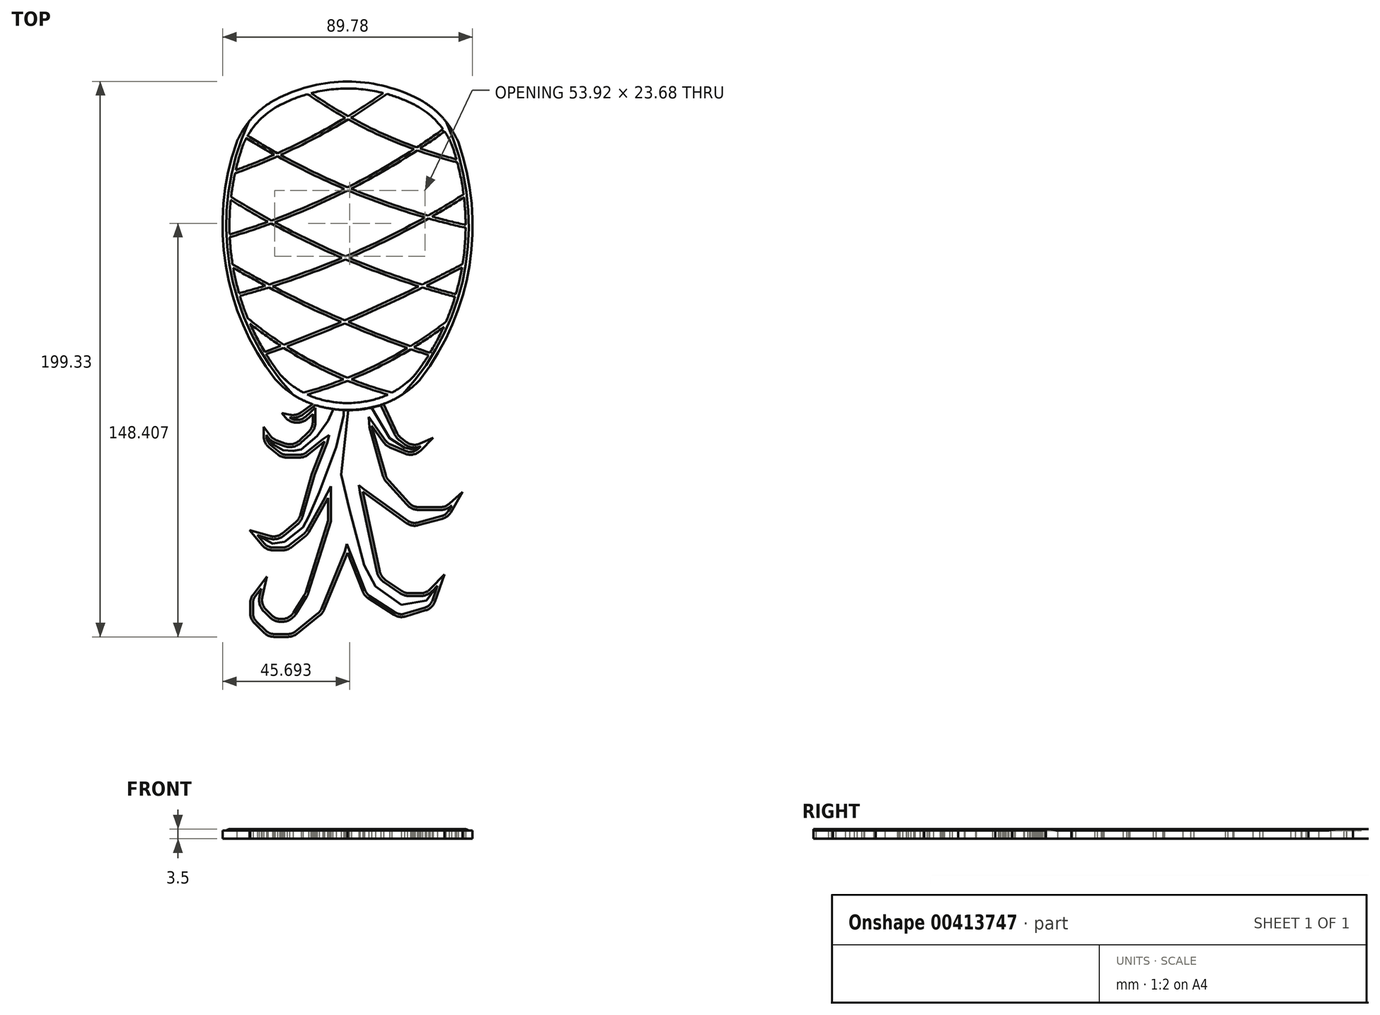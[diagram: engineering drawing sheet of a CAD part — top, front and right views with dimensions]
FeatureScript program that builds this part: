
annotation { "Feature Type Name" : "Feature", "Feature Type Description" : "" }
export const myFeature = defineFeature(function(context is Context, id is Id, definition is map)
    precondition{}
    {
        {
            var Q0;
            Q0=qCreatedBy(makeId("Top.planeOp"),FACE);
            var sketch = newSketch(context, id + "F0", { "sketchPlane" : qUnion([Q0])});
            skPoint(sketch, "E0.endSnap0", {"position": v(0.15, 19.93) * mm});
            skArc(sketch, "E1", {"start": v(-37.44, 35.3) * mm, "mid": v(-38.9, 30.75) * mm, "end": v(-40.1, 26.12) * mm});
            skPoint(sketch, "E2.center.orphan", {"position": v(0, -42.88) * mm});
            skArc(sketch, "E3", {"start": v(-24.09, -47.3) * mm, "mid": v(-20.2, -50.89) * mm, "end": v(-15.76, -53.75) * mm});
            skPoint(sketch, "E4.center.orphan", {"position": v(0, 37.68) * mm});
            skArc(sketch, "E5", {"start": v(-0.05, 55.44) * mm, "mid": v(-6.58, 55) * mm, "end": v(-13, 53.76) * mm});
            skArc(sketch, "E6", {"start": v(-23.24, 49.97) * mm, "mid": v(-30.39, 45.18) * mm, "end": v(-35.81, 38.5) * mm});
            skArc(sketch, "E7.MirrorCS", {"start": v(24.33, -47.22) * mm, "mid": v(20.41, -50.86) * mm, "end": v(15.91, -53.76) * mm});
            skArc(sketch, "E8.MirrorCS", {"start": v(37.4, 35.42) * mm, "mid": v(38.3, 32.73) * mm, "end": v(39.12, 30.01) * mm});
            skArc(sketch, "E9.MirrorCS", {"start": v(23.15, 50.05) * mm, "mid": v(29.32, 46.15) * mm, "end": v(34.32, 40.82) * mm});
            skArc(sketch, "E10.MirrorCS", {"start": v(-0.05, 55.44) * mm, "mid": v(6.47, 55.02) * mm, "end": v(12.9, 53.8) * mm});
            skArc(sketch, "E11", {"start": v(-5.74, -56.97) * mm, "mid": v(0, -57.48) * mm, "end": v(5.75, -56.99) * mm});
            skPoint(sketch, "E12.orphan", {"position": v(0.14, -57.2) * mm});
            skArc(sketch, "E13.0", {"start": v(24.2, 52.31) * mm, "mid": v(33.43, 45.75) * mm, "end": v(39.73, 36.34) * mm});
            skArc(sketch, "E13.1", {"start": v(39.73, 36.34) * mm, "mid": v(43.8, -7.95) * mm, "end": v(26.26, -48.81) * mm});
            skArc(sketch, "E13.2", {"start": v(26.26, -48.81) * mm, "mid": v(17.14, -55.93) * mm, "end": v(6.13, -59.46) * mm});
            skArc(sketch, "E13.3", {"start": v(-24.2, 52.28) * mm, "mid": v(-33.47, 45.67) * mm, "end": v(-39.77, 36.2) * mm});
            skArc(sketch, "E13.4", {"start": v(-39.77, 36.2) * mm, "mid": v(-43.7, -8.1) * mm, "end": v(-26, -48.9) * mm});
            skArc(sketch, "E13.5", {"start": v(-26, -48.9) * mm, "mid": v(-17, -55.93) * mm, "end": v(-6.13, -59.44) * mm});
            skArc(sketch, "E13.6", {"start": v(-6.13, -59.44) * mm, "mid": v(0, -59.98) * mm, "end": v(6.13, -59.46) * mm});
            skArc(sketch, "E14.0", {"start": v(-0.06, 57.94) * mm, "mid": v(13.5, 56.23) * mm, "end": v(26.25, 51.27) * mm});
            skArc(sketch, "E14.1", {"start": v(-0.06, 57.94) * mm, "mid": v(-13.62, 56.18) * mm, "end": v(-26.34, 51.18) * mm});
            skArc(sketch, "E15", {"start": v(-35.78, -27.03) * mm, "mid": v(-29.42, -31.97) * mm, "end": v(-22.8, -36.53) * mm});
            skArc(sketch, "E16", {"start": v(-41.23, -7.7) * mm, "mid": v(-34.7, -11.37) * mm, "end": v(-28.1, -14.91) * mm});
            skArc(sketch, "E17", {"start": v(-41.76, 16.52) * mm, "mid": v(-34.59, 12.19) * mm, "end": v(-27.3, 8.06) * mm});
            skArc(sketch, "E18", {"start": v(-35.81, 38.5) * mm, "mid": v(-30.5, 35.28) * mm, "end": v(-25.1, 32.2) * mm});
            skArc(sketch, "E19", {"start": v(-13, 53.76) * mm, "mid": v(-6.49, 49.47) * mm, "end": v(0.23, 45.5) * mm});
            skArc(sketch, "E20", {"start": v(-15.76, -53.75) * mm, "mid": v(-8.47, -51.53) * mm, "end": v(-1.3, -48.94) * mm});
            skArc(sketch, "E21", {"start": v(-29.7, -39.09) * mm, "mid": v(-26.83, -38.04) * mm, "end": v(-23.96, -36.97) * mm});
            skArc(sketch, "E22", {"start": v(-38.9, -18.07) * mm, "mid": v(-34.16, -16.74) * mm, "end": v(-29.45, -15.33) * mm});
            skArc(sketch, "E23", {"start": v(-42.3, 3.08) * mm, "mid": v(-35.39, 5.25) * mm, "end": v(-28.54, 7.6) * mm});
            skArc(sketch, "E24", {"start": v(-40.1, 26.12) * mm, "mid": v(-33.13, 28.8) * mm, "end": v(-26.25, 31.69) * mm});
            skArc(sketch, "E25.0", {"start": v(-34.94, -29) * mm, "mid": v(-29.55, -33.12) * mm, "end": v(-23.96, -36.97) * mm});
            skArc(sketch, "E26.0", {"start": v(-41.02, -8.97) * mm, "mid": v(-35.26, -12.2) * mm, "end": v(-29.45, -15.33) * mm});
            skArc(sketch, "E27.0", {"start": v(-41.89, 15.42) * mm, "mid": v(-35.26, 11.43) * mm, "end": v(-28.54, 7.6) * mm});
            skArc(sketch, "E28.0", {"start": v(-36.3, 37.63) * mm, "mid": v(-31.31, 34.6) * mm, "end": v(-26.25, 31.69) * mm});
            skArc(sketch, "E29.0", {"start": v(-13.57, 52.94) * mm, "mid": v(-7.26, 48.77) * mm, "end": v(-0.76, 44.9) * mm});
            skArc(sketch, "E30.0", {"start": v(-39.75, 25.18) * mm, "mid": v(-32.4, 28) * mm, "end": v(-25.16, 31.08) * mm});
            skArc(sketch, "E31.0", {"start": v(-42.01, 2.12) * mm, "mid": v(-34.66, 4.43) * mm, "end": v(-27.37, 6.97) * mm});
            skArc(sketch, "E32.0", {"start": v(-38.64, -19.03) * mm, "mid": v(-33.4, -17.56) * mm, "end": v(-28.2, -16) * mm});
            skArc(sketch, "E33.0", {"start": v(-29.17, -39.96) * mm, "mid": v(-26.04, -38.81) * mm, "end": v(-22.91, -37.65) * mm});
            skArc(sketch, "E34.0", {"start": v(-14.43, -54.41) * mm, "mid": v(-7.13, -52.13) * mm, "end": v(0.03, -49.49) * mm});
            skLineSegment(sketch, "E35", {"start": v(38.87, 29.05) * mm, "end": v(39.43, 28.9) * mm});
            skLineSegment(sketch, "E36", {"start": v(42.2, 5.49) * mm, "end": v(42.42, 5.44) * mm});
            skLineSegment(sketch, "E37", {"start": v(-13.57, 52.94) * mm, "end": v(-14.4, 53.38) * mm});
            skArc(sketch, "E38.trimOffspring", {"start": v(-14.4, 53.38) * mm, "mid": v(-19.9, 51.47) * mm, "end": v(-25.15, 48.98) * mm});
            skArc(sketch, "E39.trimOffspring", {"start": v(-25.16, 31.08) * mm, "mid": v(-13.28, 24.9) * mm, "end": v(-1.1, 19.37) * mm});
            skArc(sketch, "E40.trimOffspring", {"start": v(-25.1, 32.2) * mm, "mid": v(-12.74, 38.18) * mm, "end": v(-0.76, 44.9) * mm});
            skArc(sketch, "E41.trimOffspring", {"start": v(-24.02, 31.6) * mm, "mid": v(-12.09, 25.44) * mm, "end": v(0.15, 19.93) * mm});
            skArc(sketch, "E42.trimOffspring", {"start": v(-24.02, 31.6) * mm, "mid": v(-11.7, 37.6) * mm, "end": v(0.25, 44.35) * mm});
            skLineSegment(sketch, "E43", {"start": v(-39.75, 25.18) * mm, "end": v(-40.36, 24.97) * mm});
            skLineSegment(sketch, "E44", {"start": v(-42.01, 2.12) * mm, "end": v(-42.25, 2.05) * mm});
            skArc(sketch, "E45.trimOffspring", {"start": v(29.1, -40.32) * mm, "mid": v(26.8, -43.82) * mm, "end": v(24.33, -47.22) * mm});
            skArc(sketch, "E46.trimOffspring", {"start": v(34.54, -30.19) * mm, "mid": v(32.23, -34.89) * mm, "end": v(29.65, -39.44) * mm});
            skArc(sketch, "E47.trimOffspring", {"start": v(38.62, -19.38) * mm, "mid": v(37.12, -23.89) * mm, "end": v(35.37, -28.3) * mm});
            skArc(sketch, "E48.trimOffspring", {"start": v(41.14, -8.8) * mm, "mid": v(40.16, -13.64) * mm, "end": v(38.9, -18.42) * mm});
            skArc(sketch, "E49.trimOffspring", {"start": v(42.42, 5.44) * mm, "mid": v(42.12, -1.08) * mm, "end": v(41.34, -7.55) * mm});
            skArc(sketch, "E50.trimOffspring", {"start": v(41.83, 16.36) * mm, "mid": v(42.26, 11.42) * mm, "end": v(42.42, 6.47) * mm});
            skArc(sketch, "E51.trimOffspring", {"start": v(39.43, 28.9) * mm, "mid": v(40.75, 23.22) * mm, "end": v(41.7, 17.46) * mm});
            skArc(sketch, "E52.trimOffspring", {"start": v(34.9, 40) * mm, "mid": v(36.25, 37.77) * mm, "end": v(37.4, 35.42) * mm});
            skLineSegment(sketch, "E53", {"start": v(13.47, 52.98) * mm, "end": v(14.16, 53.47) * mm});
            skArc(sketch, "E54.trimOffspring", {"start": v(14.16, 53.47) * mm, "mid": v(19.73, 51.57) * mm, "end": v(25.06, 49.07) * mm});
            skArc(sketch, "E55.trimOffspring", {"start": v(-36.3, 37.63) * mm, "mid": v(-36.9, 36.48) * mm, "end": v(-37.44, 35.3) * mm});
            skArc(sketch, "E56.trimOffspring", {"start": v(-40.36, 24.97) * mm, "mid": v(-41.16, 20.76) * mm, "end": v(-41.76, 16.52) * mm});
            skArc(sketch, "E57.trimOffspring", {"start": v(-41.89, 15.42) * mm, "mid": v(-42.3, 9.26) * mm, "end": v(-42.3, 3.08) * mm});
            skArc(sketch, "E58.trimOffspring", {"start": v(-42.25, 2.05) * mm, "mid": v(-41.88, -2.84) * mm, "end": v(-41.23, -7.7) * mm});
            skArc(sketch, "E59.trimOffspring", {"start": v(-41.02, -8.97) * mm, "mid": v(-40.08, -13.55) * mm, "end": v(-38.9, -18.07) * mm});
            skArc(sketch, "E60.trimOffspring", {"start": v(-38.62, -19.03) * mm, "mid": v(-37.3, -23.06) * mm, "end": v(-35.78, -27.03) * mm});
            skArc(sketch, "E61.trimOffspring", {"start": v(-34.94, -29) * mm, "mid": v(-32.49, -34.13) * mm, "end": v(-29.7, -39.09) * mm});
            skArc(sketch, "E62.trimOffspring", {"start": v(-29.17, -39.96) * mm, "mid": v(-26.72, -43.7) * mm, "end": v(-24.09, -47.3) * mm});
            skArc(sketch, "E63.trimOffspring", {"start": v(-14.43, -54.41) * mm, "mid": v(-10.18, -56.02) * mm, "end": v(-5.74, -56.97) * mm});
            skPoint(sketch, "E64.trimOffspring.end.orphan", {"position": v(0.15, -64.2) * mm});
            skArc(sketch, "E65.trimOffspring", {"start": v(0.04, -48.4) * mm, "mid": v(11, -43.5) * mm, "end": v(21.54, -37.71) * mm});
            skArc(sketch, "E66.trimOffspring", {"start": v(0.03, -49.49) * mm, "mid": v(7.23, -52.16) * mm, "end": v(14.56, -54.42) * mm});
            skArc(sketch, "E67.trimOffspring", {"start": v(1.38, -48.94) * mm, "mid": v(12.28, -43.97) * mm, "end": v(22.76, -38.14) * mm});
            skArc(sketch, "E68.trimOffspring", {"start": v(1.38, -48.94) * mm, "mid": v(8.58, -51.55) * mm, "end": v(15.91, -53.76) * mm});
            skArc(sketch, "E69.trimOffspring", {"start": v(-22.8, -36.53) * mm, "mid": v(-12.5, -32.54) * mm, "end": v(-2.3, -28.34) * mm});
            skArc(sketch, "E70.trimOffspring", {"start": v(-21.74, -37.2) * mm, "mid": v(-11.34, -33.15) * mm, "end": v(-1.02, -28.88) * mm});
            skArc(sketch, "E71.trimOffspring", {"start": v(-21.74, -37.2) * mm, "mid": v(-11.1, -43.3) * mm, "end": v(0.04, -48.4) * mm});
            skArc(sketch, "E72.trimOffspring", {"start": v(-22.91, -37.65) * mm, "mid": v(-12.36, -43.77) * mm, "end": v(-1.3, -48.94) * mm});
            skArc(sketch, "E73.trimOffspring", {"start": v(23.86, -37.47) * mm, "mid": v(26.75, -38.47) * mm, "end": v(29.65, -39.44) * mm});
            skArc(sketch, "E74.trimOffspring", {"start": v(22.76, -38.14) * mm, "mid": v(25.93, -39.24) * mm, "end": v(29.1, -40.32) * mm});
            skArc(sketch, "E75.trimOffspring", {"start": v(22.64, -37.04) * mm, "mid": v(29.12, -32.84) * mm, "end": v(35.37, -28.3) * mm});
            skArc(sketch, "E76.trimOffspring", {"start": v(23.86, -37.47) * mm, "mid": v(29.28, -33.94) * mm, "end": v(34.54, -30.19) * mm});
            skArc(sketch, "E77.trimOffspring", {"start": v(0.25, -28.34) * mm, "mid": v(13.7, -22.36) * mm, "end": v(27, -16.03) * mm});
            skArc(sketch, "E78.trimOffspring", {"start": v(-1.02, -28.88) * mm, "mid": v(10.19, -33.47) * mm, "end": v(21.54, -37.71) * mm});
            skArc(sketch, "E79.trimOffspring", {"start": v(-1.02, -27.8) * mm, "mid": v(12.37, -21.87) * mm, "end": v(25.61, -15.6) * mm});
            skArc(sketch, "E80.trimOffspring", {"start": v(0.25, -28.34) * mm, "mid": v(11.38, -32.87) * mm, "end": v(22.64, -37.04) * mm});
            skArc(sketch, "E81.trimOffspring", {"start": v(-28.1, -14.91) * mm, "mid": v(-14.92, -10.45) * mm, "end": v(-1.97, -5.36) * mm});
            skArc(sketch, "E82.trimOffspring", {"start": v(-26.84, -15.57) * mm, "mid": v(-13.65, -11.05) * mm, "end": v(-0.69, -5.9) * mm});
            skArc(sketch, "E83.trimOffspring", {"start": v(-28.2, -16) * mm, "mid": v(-15.36, -22.4) * mm, "end": v(-2.3, -28.34) * mm});
            skArc(sketch, "E84.trimOffspring", {"start": v(-26.84, -15.57) * mm, "mid": v(-14.05, -21.92) * mm, "end": v(-1.02, -27.8) * mm});
            skArc(sketch, "E85.trimOffspring", {"start": v(-27.3, 8.06) * mm, "mid": v(-14.04, 13.35) * mm, "end": v(-1.1, 19.37) * mm});
            skArc(sketch, "E86.trimOffspring", {"start": v(-26.12, 7.43) * mm, "mid": v(-12.84, 12.77) * mm, "end": v(0.12, 18.86) * mm});
            skArc(sketch, "E87.trimOffspring", {"start": v(-27.37, 6.97) * mm, "mid": v(-14.82, 0.5) * mm, "end": v(-1.97, -5.36) * mm});
            skArc(sketch, "E88.trimOffspring", {"start": v(-26.12, 7.43) * mm, "mid": v(-13.55, 1) * mm, "end": v(-0.69, -4.82) * mm});
            skArc(sketch, "E89.trimOffspring", {"start": v(0.6, -5.36) * mm, "mid": v(13.64, -10.47) * mm, "end": v(26.91, -14.95) * mm});
            skArc(sketch, "E90.trimOffspring", {"start": v(0.6, -5.36) * mm, "mid": v(15.06, 1.32) * mm, "end": v(29.15, 8.78) * mm});
            skArc(sketch, "E91.trimOffspring", {"start": v(-0.69, -5.9) * mm, "mid": v(12.35, -11.06) * mm, "end": v(25.61, -15.6) * mm});
            skArc(sketch, "E92.trimOffspring", {"start": v(-0.69, -4.82) * mm, "mid": v(13.74, 1.79) * mm, "end": v(27.8, 9.16) * mm});
            skArc(sketch, "E93.trimOffspring", {"start": v(27, -16.03) * mm, "mid": v(32.8, -17.76) * mm, "end": v(38.65, -19.39) * mm});
            skArc(sketch, "E94.trimOffspring", {"start": v(28.3, -15.38) * mm, "mid": v(33.59, -16.95) * mm, "end": v(38.9, -18.42) * mm});
            skArc(sketch, "E95.trimOffspring", {"start": v(28.3, -15.38) * mm, "mid": v(34.74, -12.13) * mm, "end": v(41.14, -8.8) * mm});
            skArc(sketch, "E96.trimOffspring", {"start": v(26.91, -14.95) * mm, "mid": v(34.15, -11.3) * mm, "end": v(41.34, -7.55) * mm});
            skArc(sketch, "E97.trimOffspring", {"start": v(29.02, 9.85) * mm, "mid": v(35.4, 13.58) * mm, "end": v(41.7, 17.46) * mm});
            skArc(sketch, "E98.trimOffspring", {"start": v(29.15, 8.78) * mm, "mid": v(35.65, 7.05) * mm, "end": v(42.2, 5.49) * mm});
            skArc(sketch, "E99.trimOffspring", {"start": v(30.38, 9.48) * mm, "mid": v(36.14, 12.85) * mm, "end": v(41.83, 16.36) * mm});
            skArc(sketch, "E100.trimOffspring", {"start": v(30.38, 9.48) * mm, "mid": v(36.38, 7.9) * mm, "end": v(42.42, 6.47) * mm});
            skArc(sketch, "E101.trimOffspring", {"start": v(1.3, 19.45) * mm, "mid": v(18.5, 29.08) * mm, "end": v(34.9, 40) * mm});
            skArc(sketch, "E102.trimOffspring", {"start": v(1.3, 19.45) * mm, "mid": v(15.02, 14.25) * mm, "end": v(29.02, 9.85) * mm});
            skArc(sketch, "E103.trimOffspring", {"start": v(0.12, 18.86) * mm, "mid": v(13.82, 13.6) * mm, "end": v(27.8, 9.16) * mm});
            skArc(sketch, "E104.trimOffspring", {"start": v(0.08, 19.96) * mm, "mid": v(17.61, 29.71) * mm, "end": v(34.32, 40.82) * mm});
            skArc(sketch, "E105.trimOffspring", {"start": v(1.23, 44.94) * mm, "mid": v(7.42, 48.87) * mm, "end": v(13.47, 52.98) * mm});
            skArc(sketch, "E106.trimOffspring", {"start": v(1.23, 44.94) * mm, "mid": v(19.7, 36.27) * mm, "end": v(39.12, 30.01) * mm});
            skArc(sketch, "E107.trimOffspring", {"start": v(0.23, 45.5) * mm, "mid": v(6.63, 49.55) * mm, "end": v(12.9, 53.8) * mm});
            skArc(sketch, "E108.trimOffspring", {"start": v(0.25, 44.35) * mm, "mid": v(19.07, 35.45) * mm, "end": v(38.87, 29.05) * mm});
            skArc(sketch, "E109.trimOffspring", {"start": v(14.56, -54.42) * mm, "mid": v(10.26, -56.04) * mm, "end": v(5.75, -56.99) * mm});
            skLineSegment(sketch, "E110", {"start": v(15.91, -53.76) * mm, "end": v(14.56, -54.42) * mm});
            skLineSegment(sketch, "E111", {"start": v(-14.43, -54.41) * mm, "end": v(-15.76, -53.75) * mm});
            skLineSegment(sketch, "E112", {"start": v(-29.17, -39.96) * mm, "end": v(-29.7, -39.09) * mm});
            skLineSegment(sketch, "E113", {"start": v(-34.94, -29) * mm, "end": v(-35.78, -27.03) * mm});
            skLineSegment(sketch, "E114", {"start": v(-38.64, -19.03) * mm, "end": v(-38.9, -18.07) * mm});
            skLineSegment(sketch, "E115", {"start": v(-41.02, -8.97) * mm, "end": v(-41.23, -7.7) * mm});
            skLineSegment(sketch, "E116", {"start": v(-42.25, 2.05) * mm, "end": v(-42.3, 3.08) * mm});
            skLineSegment(sketch, "E117", {"start": v(-41.89, 15.42) * mm, "end": v(-41.76, 16.52) * mm});
            skLineSegment(sketch, "E118", {"start": v(-40.36, 24.97) * mm, "end": v(-40.1, 26.12) * mm});
            skLineSegment(sketch, "E119", {"start": v(-36.3, 37.63) * mm, "end": v(-35.81, 38.5) * mm});
            skLineSegment(sketch, "E120", {"start": v(-14.4, 53.38) * mm, "end": v(-13, 53.76) * mm});
            skLineSegment(sketch, "E121", {"start": v(12.9, 53.8) * mm, "end": v(14.16, 53.47) * mm});
            skLineSegment(sketch, "E122", {"start": v(34.32, 40.82) * mm, "end": v(34.9, 40) * mm});
            skLineSegment(sketch, "E123", {"start": v(39.12, 30.01) * mm, "end": v(39.43, 28.9) * mm});
            skLineSegment(sketch, "E124", {"start": v(41.7, 17.46) * mm, "end": v(41.83, 16.36) * mm});
            skLineSegment(sketch, "E125", {"start": v(42.42, 6.47) * mm, "end": v(42.42, 5.44) * mm});
            skLineSegment(sketch, "E126", {"start": v(41.34, -7.55) * mm, "end": v(41.14, -8.8) * mm});
            skLineSegment(sketch, "E127", {"start": v(38.62, -19.38) * mm, "end": v(38.9, -18.42) * mm});
            skLineSegment(sketch, "E128", {"start": v(35.37, -28.3) * mm, "end": v(34.54, -30.19) * mm});
            skLineSegment(sketch, "E129", {"start": v(29.65, -39.44) * mm, "end": v(29.1, -40.32) * mm});
            skSolve(sketch);
        }
        {
            var Q0;
            Q0 = qSketchRegion(id + "F0", true);
            var Q1;
            Q1=makeQuery(id+"F0.imprint","IMPRINT",FACE,{"disambiguationData":[TD([[makeQuery(id+"F0.imprint","IMPRINT",EDGE,{"derivedFrom":sQuery(id+"F0.wireOp",EDGE,"E1")}),-1.0]])]});
            var Q2;
            Q2=makeQuery(id+"F0.imprint","IMPRINT",FACE,{"disambiguationData":[TD([[makeQuery(id+"F0.imprint","IMPRINT",EDGE,{"derivedFrom":sQuery(id+"F0.wireOp",EDGE,"E15")}),-1.0]])]});
            var Q3;
            {var subQ5=sQuery(id+"F0.wireOp",EDGE,"E122");Q3=makeQuery(id+"F0.imprint","IMPRINT",FACE,{"disambiguationData":[TD([[makeQuery(id+"F0.imprint","IMPRINT",EDGE,{"derivedFrom":subQ5}),-1.0]])]});}
            var Q4;
            {var subQ0=sQuery(id+"F0.wireOp",EDGE,"E108.trimOffspring");var subQ1=sQuery(id+"F0.wireOp",EDGE,"E101.trimOffspring");var subQ2=makeQuery(id+"F0.imprint","INTERSECT",VERTEX,{"derivedFrom":[subQ1,subQ0]});Q4=makeQuery(id+"F0.imprint","IMPRINT",FACE,{"disambiguationData":[TD([[makeQuery(id+"F0.imprint","IMPRINT",EDGE,{"disambiguationData":[TD([[subQ2,-1.0]])],"derivedFrom":subQ1}),1.0]])]});}
            var Q5;
            {var subQ6=sQuery(id+"F0.wireOp",EDGE,"E35");Q5=makeQuery(id+"F0.imprint","IMPRINT",FACE,{"disambiguationData":[TD([[makeQuery(id+"F0.imprint","IMPRINT",EDGE,{"derivedFrom":subQ6}),1.0]])]});}
            extrude(context, id + "F1", {"entities" : qUnion([Q0, Q1, Q2, Q3, Q4, Q5]), "depth" : 3.5 * mm});
        }
        {
            var Q0;
            {var subQ1=sQuery(id+"F0.wireOp",EDGE,"E18");Q0=makeQuery(id+"F0.imprint","IMPRINT",FACE,{"disambiguationData":[TD([[makeQuery(id+"F0.imprint","IMPRINT",EDGE,{"derivedFrom":subQ1}),1.0]])]});}
            var Q1;
            Q1=makeQuery(id+"F0.imprint","IMPRINT",FACE,{"disambiguationData":[TD([[makeQuery(id+"F0.imprint","IMPRINT",EDGE,{"derivedFrom":sQuery(id+"F0.wireOp",EDGE,"E5")}),1.0]])]});
            var Q2;
            {var subQ5=sQuery(id+"F0.wireOp",EDGE,"E53");Q2=makeQuery(id+"F0.imprint","IMPRINT",FACE,{"disambiguationData":[TD([[makeQuery(id+"F0.imprint","IMPRINT",EDGE,{"derivedFrom":subQ5}),-1.0]])]});}
            var Q3;
            {var subQ0=sQuery(id+"F0.wireOp",EDGE,"E42.trimOffspring");Q3=makeQuery(id+"F0.imprint","IMPRINT",FACE,{"disambiguationData":[TD([[makeQuery(id+"F0.imprint","IMPRINT",EDGE,{"derivedFrom":subQ0}),-1.0]])]});}
            var Q4;
            {var subQ4=sQuery(id+"F0.wireOp",EDGE,"E35");Q4=makeQuery(id+"F0.imprint","IMPRINT",FACE,{"disambiguationData":[TD([[makeQuery(id+"F0.imprint","IMPRINT",EDGE,{"derivedFrom":subQ4}),-1.0]])]});}
            var Q5;
            {var subQ0=sQuery(id+"F0.wireOp",EDGE,"E8.MirrorCS");Q5=makeQuery(id+"F0.imprint","IMPRINT",FACE,{"disambiguationData":[TD([[makeQuery(id+"F0.imprint","IMPRINT",EDGE,{"derivedFrom":subQ0}),-1.0]])]});}
            var Q6;
            Q6=makeQuery(id+"F0.imprint","IMPRINT",FACE,{"disambiguationData":[TD([[makeQuery(id+"F0.imprint","IMPRINT",EDGE,{"derivedFrom":sQuery(id+"F0.wireOp",EDGE,"E1")}),1.0]])]});
            var Q7;
            Q7=makeQuery(id+"F0.imprint","IMPRINT",FACE,{"disambiguationData":[TD([[makeQuery(id+"F0.imprint","IMPRINT",EDGE,{"derivedFrom":sQuery(id+"F0.wireOp",EDGE,"E23")}),1.0]])]});
            var Q8;
            Q8=makeQuery(id+"F0.imprint","IMPRINT",FACE,{"disambiguationData":[TD([[makeQuery(id+"F0.imprint","IMPRINT",EDGE,{"derivedFrom":sQuery(id+"F0.wireOp",EDGE,"E16")}),1.0]])]});
            var Q9;
            Q9=makeQuery(id+"F0.imprint","IMPRINT",FACE,{"disambiguationData":[TD([[makeQuery(id+"F0.imprint","IMPRINT",EDGE,{"derivedFrom":sQuery(id+"F0.wireOp",EDGE,"E22")}),1.0]])]});
            var Q10;
            Q10=makeQuery(id+"F0.imprint","IMPRINT",FACE,{"disambiguationData":[TD([[makeQuery(id+"F0.imprint","IMPRINT",EDGE,{"derivedFrom":sQuery(id+"F0.wireOp",EDGE,"E15")}),1.0]])]});
            var Q11;
            Q11=makeQuery(id+"F0.imprint","IMPRINT",FACE,{"disambiguationData":[TD([[makeQuery(id+"F0.imprint","IMPRINT",EDGE,{"derivedFrom":sQuery(id+"F0.wireOp",EDGE,"E21")}),1.0]])]});
            var Q12;
            {var subQ0=sQuery(id+"F0.wireOp",EDGE,"E47.trimOffspring");Q12=makeQuery(id+"F0.imprint","IMPRINT",FACE,{"disambiguationData":[TD([[makeQuery(id+"F0.imprint","IMPRINT",EDGE,{"derivedFrom":subQ0}),-1.0]])]});}
            var Q13;
            Q13=makeQuery(id+"F0.imprint","IMPRINT",FACE,{"disambiguationData":[TD([[makeQuery(id+"F0.imprint","IMPRINT",EDGE,{"derivedFrom":sQuery(id+"F0.wireOp",EDGE,"E79.trimOffspring")}),1.0]])]});
            var Q14;
            Q14=makeQuery(id+"F0.imprint","IMPRINT",FACE,{"disambiguationData":[TD([[makeQuery(id+"F0.imprint","IMPRINT",EDGE,{"derivedFrom":sQuery(id+"F0.wireOp",EDGE,"E36")}),-1.0]])]});
            var Q15;
            Q15=makeQuery(id+"F0.imprint","IMPRINT",FACE,{"disambiguationData":[TD([[makeQuery(id+"F0.imprint","IMPRINT",EDGE,{"derivedFrom":sQuery(id+"F0.wireOp",EDGE,"E86.trimOffspring")}),-1.0]])]});
            var Q16;
            Q16=makeQuery(id+"F0.imprint","IMPRINT",FACE,{"disambiguationData":[TD([[makeQuery(id+"F0.imprint","IMPRINT",EDGE,{"derivedFrom":sQuery(id+"F0.wireOp",EDGE,"E17")}),1.0]])]});
            var Q17;
            Q17=makeQuery(id+"F0.imprint","IMPRINT",FACE,{"disambiguationData":[TD([[makeQuery(id+"F0.imprint","IMPRINT",EDGE,{"derivedFrom":sQuery(id+"F0.wireOp",EDGE,"E46.trimOffspring")}),-1.0]])]});
            var Q18;
            Q18=makeQuery(id+"F0.imprint","IMPRINT",FACE,{"disambiguationData":[TD([[makeQuery(id+"F0.imprint","IMPRINT",EDGE,{"derivedFrom":sQuery(id+"F0.wireOp",EDGE,"E48.trimOffspring")}),-1.0]])]});
            var Q19;
            Q19=makeQuery(id+"F0.imprint","IMPRINT",FACE,{"disambiguationData":[TD([[makeQuery(id+"F0.imprint","IMPRINT",EDGE,{"derivedFrom":sQuery(id+"F0.wireOp",EDGE,"E50.trimOffspring")}),-1.0]])]});
            var Q20;
            Q20=makeQuery(id+"F0.imprint","IMPRINT",FACE,{"disambiguationData":[TD([[makeQuery(id+"F0.imprint","IMPRINT",EDGE,{"derivedFrom":sQuery(id+"F0.wireOp",EDGE,"E3")}),1.0]])]});
            var Q21;
            Q21=makeQuery(id+"F0.imprint","IMPRINT",FACE,{"disambiguationData":[TD([[makeQuery(id+"F0.imprint","IMPRINT",EDGE,{"derivedFrom":sQuery(id+"F0.wireOp",EDGE,"E65.trimOffspring")}),1.0]])]});
            var Q22;
            Q22=makeQuery(id+"F0.imprint","IMPRINT",FACE,{"disambiguationData":[TD([[makeQuery(id+"F0.imprint","IMPRINT",EDGE,{"derivedFrom":sQuery(id+"F0.wireOp",EDGE,"E7.MirrorCS")}),-1.0]])]});
            var Q23;
            Q23=makeQuery(id+"F0.imprint","IMPRINT",FACE,{"disambiguationData":[TD([[makeQuery(id+"F0.imprint","IMPRINT",EDGE,{"derivedFrom":sQuery(id+"F0.wireOp",EDGE,"E11")}),1.0]])]});
            extrude(context, id + "F2", {"entities" : qUnion([Q0, Q1, Q2, Q3, Q4, Q5, Q6, Q7, Q8, Q9, Q10, Q11, Q12, Q13, Q14, Q15, Q16, Q17, Q18, Q19, Q20, Q21, Q22, Q23]), "depth" : 3 * mm});
        }
        {
            var Q0;
            Q0=makeQuery(id+"F1.opExtrude","CAP_EDGE",EDGE,{"disambiguationData":[OSD([sQuery(id+"F0.wireOp",EDGE,"E13.1")])],"isStart":false});
            fillet(context, id + "F3", {"entities" : qUnion([Q0]), "radius" : 3 * mm, "tangentPropagation" : true, "allowEdgeOverflow" : false});
        }
        {
            var Q0;
            Q0=makeQuery(id+"F1.opExtrude","CAP_EDGE",EDGE,{"disambiguationData":[OSD([sQuery(id+"F0.wireOp",EDGE,"E13.4")])],"isStart":false});
            fillet(context, id + "F4", {"entities" : qUnion([Q0]), "radius" : 3 * mm, "tangentPropagation" : true, "allowEdgeOverflow" : false});
        }
        {
            var Q0;
            Q0=qCreatedBy(makeId("Top.planeOp"),FACE);
            var sketch = newSketch(context, id + "F5", { "sketchPlane" : qUnion([Q0])});
            skArc(sketch, "E130", {"start": v(-12.47, -57.76) * mm, "mid": v(0.25, -60.04) * mm, "end": v(12.98, -57.88) * mm});
            skLineSegment(sketch, "E131", {"start": v(12.98, -57.88) * mm, "end": v(17.84, -68.25) * mm});
            skLineSegment(sketch, "E132", {"start": v(19.33, -70.1) * mm, "end": v(21.06, -71.42) * mm});
            skLineSegment(sketch, "E133", {"start": v(26.1, -72.04) * mm, "end": v(30.81, -70) * mm});
            skLineSegment(sketch, "E134", {"start": v(30.81, -70) * mm, "end": v(26.14, -74.6) * mm});
            skLineSegment(sketch, "E135", {"start": v(20.7, -75.64) * mm, "end": v(15.13, -73.32) * mm});
            skLineSegment(sketch, "E136", {"start": v(13, -71.62) * mm, "end": v(8.7, -65.63) * mm});
            skLineSegment(sketch, "E137", {"start": v(8.7, -65.63) * mm, "end": v(13.74, -83.35) * mm});
            skLineSegment(sketch, "E138", {"start": v(14.85, -85.34) * mm, "end": v(21.99, -93.22) * mm});
            skLineSegment(sketch, "E139", {"start": v(25.7, -94.86) * mm, "end": v(33.32, -94.86) * mm});
            skLineSegment(sketch, "E140", {"start": v(36.65, -93.6) * mm, "end": v(41.36, -89.4) * mm});
            skLineSegment(sketch, "E141", {"start": v(41.36, -89.4) * mm, "end": v(37.09, -96.73) * mm});
            skLineSegment(sketch, "E142", {"start": v(34.05, -99.04) * mm, "end": v(25.34, -101.35) * mm});
            skLineSegment(sketch, "E143", {"start": v(21.14, -100.58) * mm, "end": v(5.46, -89.3) * mm});
            skLineSegment(sketch, "E144", {"start": v(5.46, -89.3) * mm, "end": v(11.6, -117.88) * mm});
            skLineSegment(sketch, "E145", {"start": v(13.66, -120.96) * mm, "end": v(19.41, -124.89) * mm});
            skLineSegment(sketch, "E146", {"start": v(22.23, -125.76) * mm, "end": v(26.18, -125.76) * mm});
            skLineSegment(sketch, "E147", {"start": v(29.78, -124.22) * mm, "end": v(34.77, -119.03) * mm});
            skLineSegment(sketch, "E148", {"start": v(34.77, -119.03) * mm, "end": v(31.4, -128.7) * mm});
            skLineSegment(sketch, "E149", {"start": v(28.14, -131.84) * mm, "end": v(20.83, -134.08) * mm});
            skLineSegment(sketch, "E150", {"start": v(16.65, -133.5) * mm, "end": v(7.4, -127.5) * mm});
            skLineSegment(sketch, "E151", {"start": v(5.46, -125.13) * mm, "end": v(0, -111.21) * mm});
            skLineSegment(sketch, "E152", {"start": v(0, -111.21) * mm, "end": v(-8.44, -131.75) * mm});
            skLineSegment(sketch, "E153", {"start": v(-9.95, -133.76) * mm, "end": v(-18.15, -140.3) * mm});
            skLineSegment(sketch, "E154", {"start": v(-21.27, -141.39) * mm, "end": v(-26.4, -141.39) * mm});
            skLineSegment(sketch, "E155", {"start": v(-29.92, -139.95) * mm, "end": v(-33.4, -136.52) * mm});
            skLineSegment(sketch, "E156", {"start": v(-34.9, -132.95) * mm, "end": v(-34.9, -129.3) * mm});
            skLineSegment(sketch, "E157", {"start": v(-33.88, -126.28) * mm, "end": v(-28.98, -119.8) * mm});
            skLineSegment(sketch, "E158", {"start": v(-28.98, -119.8) * mm, "end": v(-30.57, -127.08) * mm});
            skLineSegment(sketch, "E159", {"start": v(-29.18, -131.73) * mm, "end": v(-27.24, -133.62) * mm});
            skLineSegment(sketch, "E160", {"start": v(-23.75, -135.03) * mm, "end": v(-23.6, -135.03) * mm});
            skLineSegment(sketch, "E161", {"start": v(-19.35, -132.67) * mm, "end": v(-15.5, -126.46) * mm});
            skLineSegment(sketch, "E162", {"start": v(-14.97, -125.31) * mm, "end": v(-6.97, -99.73) * mm});
            skLineSegment(sketch, "E163", {"start": v(-6.97, -99.73) * mm, "end": v(-6.97, -91.59) * mm});
            skLineSegment(sketch, "E164", {"start": v(-6.97, -91.59) * mm, "end": v(-13.82, -103.79) * mm});
            skLineSegment(sketch, "E165", {"start": v(-15.1, -105.28) * mm, "end": v(-20.22, -109.28) * mm});
            skLineSegment(sketch, "E166", {"start": v(-23.3, -110.33) * mm, "end": v(-26.74, -110.33) * mm});
            skLineSegment(sketch, "E167", {"start": v(-30.58, -108.54) * mm, "end": v(-35.15, -103.06) * mm});
            skLineSegment(sketch, "E168", {"start": v(-35.15, -103.06) * mm, "end": v(-27.87, -105.16) * mm});
            skPoint(sketch, "E168.endSnap0", {"position": v(-25.33, -110.33) * mm});
            skLineSegment(sketch, "E169", {"start": v(-23.3, -104.2) * mm, "end": v(-18.65, -100.33) * mm});
            skLineSegment(sketch, "E170", {"start": v(-17.04, -97.85) * mm, "end": v(-12.78, -82.86) * mm});
            skLineSegment(sketch, "E171", {"start": v(-12.78, -82.86) * mm, "end": v(-8.19, -71.23) * mm});
            skLineSegment(sketch, "E172", {"start": v(-8.19, -71.23) * mm, "end": v(-14.05, -75.94) * mm});
            skPoint(sketch, "E172.endSnap0", {"position": v(-10.48, -77.04) * mm});
            skLineSegment(sketch, "E173", {"start": v(-17.18, -77.04) * mm, "end": v(-21.87, -77.04) * mm});
            skLineSegment(sketch, "E174", {"start": v(-25.03, -75.92) * mm, "end": v(-28.2, -73.34) * mm});
            skLineSegment(sketch, "E175", {"start": v(-30.05, -69.46) * mm, "end": v(-30.05, -65.95) * mm});
            skLineSegment(sketch, "E176", {"start": v(-30.05, -65.95) * mm, "end": v(-27.72, -69.1) * mm});
            skPoint(sketch, "E176.endSnap0", {"position": v(-26.85, -74.44) * mm});
            skLineSegment(sketch, "E177", {"start": v(-25.47, -70.82) * mm, "end": v(-22.45, -71.96) * mm});
            skPoint(sketch, "E177.endSnap0", {"position": v(-19.54, -77.04) * mm});
            skLineSegment(sketch, "E178", {"start": v(-17.26, -70.93) * mm, "end": v(-14.05, -67.92) * mm});
            skLineSegment(sketch, "E179", {"start": v(-12.47, -64.27) * mm, "end": v(-12.47, -61.48) * mm});
            skLineSegment(sketch, "E180", {"start": v(-12.47, -61.48) * mm, "end": v(-14.6, -63.3) * mm});
            skPoint(sketch, "E180.endSnap0", {"position": v(-16, -69.75) * mm});
            skLineSegment(sketch, "E181", {"start": v(-17.84, -64.48) * mm, "end": v(-18.42, -64.48) * mm});
            skLineSegment(sketch, "E182", {"start": v(-22.2, -62.75) * mm, "end": v(-23.6, -61.11) * mm});
            skLineSegment(sketch, "E183", {"start": v(-23.6, -61.11) * mm, "end": v(-20.5, -61.7) * mm});
            skPoint(sketch, "E183.endSnap0", {"position": v(-18.35, -64.48) * mm});
            skLineSegment(sketch, "E184", {"start": v(-16.6, -60.81) * mm, "end": v(-12.47, -57.76) * mm});
            skPoint(sketch, "E185.visualSharp", {"position": v(23.4, -73.2) * mm});
            skArc(sketch, "E185.filletArc", {"start": v(21.06, -71.42) * mm, "mid": v(23.5, -72.41) * mm, "end": v(26.1, -72.04) * mm});
            skPoint(sketch, "E186.visualSharp", {"position": v(18.36, -69.36) * mm});
            skArc(sketch, "E186.filletArc", {"start": v(17.84, -68.25) * mm, "mid": v(18.48, -69.26) * mm, "end": v(19.33, -70.1) * mm});
            skPoint(sketch, "E187.visualSharp", {"position": v(23.77, -76.93) * mm});
            skArc(sketch, "E187.filletArc", {"start": v(20.7, -75.64) * mm, "mid": v(23.58, -75.94) * mm, "end": v(26.14, -74.6) * mm});
            skPoint(sketch, "E188.visualSharp", {"position": v(13.82, -72.77) * mm});
            skArc(sketch, "E188.filletArc", {"start": v(13, -71.62) * mm, "mid": v(13.94, -72.62) * mm, "end": v(15.13, -73.32) * mm});
            skPoint(sketch, "E189.visualSharp", {"position": v(-16, -64.48) * mm});
            skArc(sketch, "E189.filletArc", {"start": v(-17.84, -64.48) * mm, "mid": v(-16.11, -64.18) * mm, "end": v(-14.6, -63.3) * mm});
            skPoint(sketch, "E190.visualSharp", {"position": v(-18.35, -62.11) * mm});
            skArc(sketch, "E190.filletArc", {"start": v(-20.5, -61.7) * mm, "mid": v(-18.46, -61.67) * mm, "end": v(-16.6, -60.81) * mm});
            skPoint(sketch, "E191.visualSharp", {"position": v(-20.7, -64.48) * mm});
            skArc(sketch, "E191.filletArc", {"start": v(-22.2, -62.75) * mm, "mid": v(-20.5, -64.03) * mm, "end": v(-18.42, -64.48) * mm});
            skPoint(sketch, "E192.visualSharp", {"position": v(-26.85, -70.3) * mm});
            skArc(sketch, "E192.filletArc", {"start": v(-27.72, -69.1) * mm, "mid": v(-26.72, -70.13) * mm, "end": v(-25.47, -70.82) * mm});
            skPoint(sketch, "E193.visualSharp", {"position": v(-19.54, -73.06) * mm});
            skArc(sketch, "E193.filletArc", {"start": v(-22.45, -71.96) * mm, "mid": v(-19.7, -72.19) * mm, "end": v(-17.26, -70.93) * mm});
            skPoint(sketch, "E194.visualSharp", {"position": v(-12.47, -66.43) * mm});
            skArc(sketch, "E194.filletArc", {"start": v(-14.05, -67.92) * mm, "mid": v(-12.88, -66.26) * mm, "end": v(-12.47, -64.27) * mm});
            skPoint(sketch, "E195.visualSharp", {"position": v(-30.05, -71.83) * mm});
            skArc(sketch, "E195.filletArc", {"start": v(-30.05, -69.46) * mm, "mid": v(-29.56, -71.6) * mm, "end": v(-28.2, -73.34) * mm});
            skPoint(sketch, "E196.visualSharp", {"position": v(-23.65, -77.04) * mm});
            skArc(sketch, "E196.filletArc", {"start": v(-25.03, -75.92) * mm, "mid": v(-23.55, -76.75) * mm, "end": v(-21.87, -77.04) * mm});
            skPoint(sketch, "E197.visualSharp", {"position": v(-15.42, -77.04) * mm});
            skArc(sketch, "E197.filletArc", {"start": v(-17.18, -77.04) * mm, "mid": v(-15.52, -76.76) * mm, "end": v(-14.05, -75.94) * mm});
            skPoint(sketch, "E198.visualSharp", {"position": v(-17.47, -99.34) * mm});
            skArc(sketch, "E198.filletArc", {"start": v(-18.65, -100.33) * mm, "mid": v(-17.66, -99.21) * mm, "end": v(-17.04, -97.85) * mm});
            skPoint(sketch, "E199.visualSharp", {"position": v(-25.33, -105.89) * mm});
            skArc(sketch, "E199.filletArc", {"start": v(-27.87, -105.16) * mm, "mid": v(-25.46, -105.24) * mm, "end": v(-23.3, -104.2) * mm});
            skPoint(sketch, "E200.visualSharp", {"position": v(-29.08, -110.33) * mm});
            skArc(sketch, "E200.filletArc", {"start": v(-30.58, -108.54) * mm, "mid": v(-28.86, -109.86) * mm, "end": v(-26.74, -110.33) * mm});
            skPoint(sketch, "E201.visualSharp", {"position": v(-21.57, -110.33) * mm});
            skArc(sketch, "E201.filletArc", {"start": v(-23.3, -110.33) * mm, "mid": v(-21.67, -110.06) * mm, "end": v(-20.22, -109.28) * mm});
            skPoint(sketch, "E202.visualSharp", {"position": v(-14.3, -104.67) * mm});
            skArc(sketch, "E202.filletArc", {"start": v(-15.1, -105.28) * mm, "mid": v(-14.38, -104.6) * mm, "end": v(-13.82, -103.79) * mm});
            skPoint(sketch, "E203.visualSharp", {"position": v(35.22, -94.86) * mm});
            skArc(sketch, "E203.filletArc", {"start": v(33.32, -94.86) * mm, "mid": v(35.1, -94.53) * mm, "end": v(36.65, -93.6) * mm});
            skPoint(sketch, "E204.visualSharp", {"position": v(36.05, -98.51) * mm});
            skArc(sketch, "E204.filletArc", {"start": v(34.05, -99.04) * mm, "mid": v(35.8, -98.19) * mm, "end": v(37.09, -96.73) * mm});
            skPoint(sketch, "E205.visualSharp", {"position": v(23.05, -101.96) * mm});
            skArc(sketch, "E205.filletArc", {"start": v(21.14, -100.58) * mm, "mid": v(23.15, -101.44) * mm, "end": v(25.34, -101.35) * mm});
            skPoint(sketch, "E206.visualSharp", {"position": v(23.48, -94.86) * mm});
            skArc(sketch, "E206.filletArc", {"start": v(21.99, -93.22) * mm, "mid": v(23.67, -94.43) * mm, "end": v(25.7, -94.86) * mm});
            skPoint(sketch, "E207.visualSharp", {"position": v(14.06, -84.47) * mm});
            skArc(sketch, "E207.filletArc", {"start": v(13.74, -83.35) * mm, "mid": v(14.18, -84.4) * mm, "end": v(14.85, -85.34) * mm});
            skPoint(sketch, "E208.visualSharp", {"position": v(28.3, -125.76) * mm});
            skArc(sketch, "E208.filletArc", {"start": v(26.18, -125.76) * mm, "mid": v(28.14, -125.36) * mm, "end": v(29.78, -124.22) * mm});
            skPoint(sketch, "E209.visualSharp", {"position": v(30.57, -131.1) * mm});
            skArc(sketch, "E209.filletArc", {"start": v(28.14, -131.84) * mm, "mid": v(30.15, -130.66) * mm, "end": v(31.4, -128.7) * mm});
            skPoint(sketch, "E210.visualSharp", {"position": v(20.69, -125.76) * mm});
            skArc(sketch, "E210.filletArc", {"start": v(19.41, -124.89) * mm, "mid": v(20.76, -125.53) * mm, "end": v(22.23, -125.76) * mm});
            skPoint(sketch, "E211.visualSharp", {"position": v(18.6, -134.76) * mm});
            skArc(sketch, "E211.filletArc", {"start": v(16.65, -133.5) * mm, "mid": v(18.68, -134.25) * mm, "end": v(20.83, -134.08) * mm});
            skPoint(sketch, "E212.visualSharp", {"position": v(12, -119.83) * mm});
            skArc(sketch, "E212.filletArc", {"start": v(11.6, -117.88) * mm, "mid": v(12.33, -119.62) * mm, "end": v(13.66, -120.96) * mm});
            skPoint(sketch, "E213.visualSharp", {"position": v(-15.16, -125.92) * mm});
            skArc(sketch, "E213.filletArc", {"start": v(-15.5, -126.46) * mm, "mid": v(-15.2, -125.9) * mm, "end": v(-14.97, -125.31) * mm});
            skPoint(sketch, "E214.visualSharp", {"position": v(-8.94, -132.95) * mm});
            skArc(sketch, "E214.filletArc", {"start": v(-9.95, -133.76) * mm, "mid": v(-9.07, -132.85) * mm, "end": v(-8.44, -131.75) * mm});
            skPoint(sketch, "E215.visualSharp", {"position": v(-19.52, -141.39) * mm});
            skArc(sketch, "E215.filletArc", {"start": v(-21.27, -141.39) * mm, "mid": v(-19.62, -141.1) * mm, "end": v(-18.15, -140.3) * mm});
            skPoint(sketch, "E216.visualSharp", {"position": v(-28.46, -141.39) * mm});
            skArc(sketch, "E216.filletArc", {"start": v(-29.92, -139.95) * mm, "mid": v(-28.3, -141.02) * mm, "end": v(-26.4, -141.39) * mm});
            skPoint(sketch, "E217.visualSharp", {"position": v(-25.78, -135.03) * mm});
            skArc(sketch, "E217.filletArc", {"start": v(-27.24, -133.62) * mm, "mid": v(-25.63, -134.67) * mm, "end": v(-23.75, -135.03) * mm});
            skPoint(sketch, "E218.visualSharp", {"position": v(-31.17, -129.8) * mm});
            skArc(sketch, "E218.filletArc", {"start": v(-30.57, -127.08) * mm, "mid": v(-30.48, -129.58) * mm, "end": v(-29.18, -131.73) * mm});
            skPoint(sketch, "E219.visualSharp", {"position": v(-34.9, -135.05) * mm});
            skArc(sketch, "E219.filletArc", {"start": v(-34.9, -132.95) * mm, "mid": v(-34.5, -134.88) * mm, "end": v(-33.4, -136.52) * mm});
            skPoint(sketch, "E220.visualSharp", {"position": v(-34.9, -127.62) * mm});
            skArc(sketch, "E220.filletArc", {"start": v(-33.88, -126.28) * mm, "mid": v(-34.64, -127.7) * mm, "end": v(-34.9, -129.3) * mm});
            skPoint(sketch, "E221.visualSharp", {"position": v(-20.82, -135.03) * mm});
            skArc(sketch, "E221.filletArc", {"start": v(-23.6, -135.03) * mm, "mid": v(-21.17, -134.4) * mm, "end": v(-19.35, -132.67) * mm});
            skPoint(sketch, "E222.visualSharp", {"position": v(6.05, -126.63) * mm});
            skArc(sketch, "E222.filletArc", {"start": v(5.46, -125.13) * mm, "mid": v(6.24, -126.47) * mm, "end": v(7.4, -127.5) * mm});
            skLineSegment(sketch, "E223.0", {"start": v(13.8, -71.03) * mm, "end": v(10.05, -65.79) * mm});
            skArc(sketch, "E223.1", {"start": v(13.8, -71.03) * mm, "mid": v(14.57, -71.83) * mm, "end": v(15.52, -72.4) * mm});
            skLineSegment(sketch, "E223.2", {"start": v(21.09, -74.72) * mm, "end": v(15.52, -72.4) * mm});
            skArc(sketch, "E223.3", {"start": v(21.09, -74.72) * mm, "mid": v(23.39, -74.96) * mm, "end": v(25.44, -73.88) * mm});
            skLineSegment(sketch, "E223.4", {"start": v(26.3, -73.04) * mm, "end": v(25.44, -73.88) * mm});
            skLineSegment(sketch, "E223.5", {"start": v(12.08, -58.3) * mm, "end": v(16.94, -68.67) * mm});
            skArc(sketch, "E223.6", {"start": v(16.94, -68.67) * mm, "mid": v(17.7, -69.9) * mm, "end": v(18.72, -70.9) * mm});
            skLineSegment(sketch, "E223.7", {"start": v(18.72, -70.9) * mm, "end": v(20.46, -72.22) * mm});
            skArc(sketch, "E223.8", {"start": v(20.46, -72.22) * mm, "mid": v(23.27, -73.4) * mm, "end": v(26.3, -73.04) * mm});
            skLineSegment(sketch, "E224.0", {"start": v(21.72, -99.77) * mm, "end": v(6.04, -88.49) * mm});
            skArc(sketch, "E224.1", {"start": v(21.25, -93.9) * mm, "mid": v(23.26, -95.35) * mm, "end": v(25.7, -95.86) * mm});
            skLineSegment(sketch, "E224.2", {"start": v(14.1, -86.01) * mm, "end": v(21.25, -93.9) * mm});
            skArc(sketch, "E224.3", {"start": v(12.78, -83.62) * mm, "mid": v(13.3, -84.9) * mm, "end": v(14.1, -86.01) * mm});
            skLineSegment(sketch, "E224.4", {"start": v(8.11, -67.2) * mm, "end": v(12.78, -83.62) * mm});
            skLineSegment(sketch, "E224.5", {"start": v(25.7, -95.86) * mm, "end": v(33.32, -95.86) * mm});
            skArc(sketch, "E224.6", {"start": v(33.32, -95.86) * mm, "mid": v(35.47, -95.46) * mm, "end": v(37.33, -94.32) * mm});
            skLineSegment(sketch, "E224.7", {"start": v(37.33, -94.32) * mm, "end": v(36.22, -96.22) * mm});
            skArc(sketch, "E224.8", {"start": v(33.8, -98.07) * mm, "mid": v(35.2, -97.39) * mm, "end": v(36.22, -96.22) * mm});
            skLineSegment(sketch, "E224.9", {"start": v(33.8, -98.07) * mm, "end": v(25.08, -100.39) * mm});
            skArc(sketch, "E224.10", {"start": v(21.72, -99.77) * mm, "mid": v(23.33, -100.45) * mm, "end": v(25.08, -100.39) * mm});
            skLineSegment(sketch, "E225.0", {"start": v(6.4, -124.77) * mm, "end": v(0.93, -110.85) * mm});
            skArc(sketch, "E225.1", {"start": v(6.4, -124.77) * mm, "mid": v(7.02, -125.84) * mm, "end": v(7.94, -126.66) * mm});
            skLineSegment(sketch, "E225.2", {"start": v(17.2, -132.65) * mm, "end": v(7.94, -126.66) * mm});
            skArc(sketch, "E225.3", {"start": v(17.2, -132.65) * mm, "mid": v(18.82, -133.26) * mm, "end": v(20.54, -133.12) * mm});
            skArc(sketch, "E225.4", {"start": v(18.85, -125.71) * mm, "mid": v(20.46, -126.49) * mm, "end": v(22.23, -126.76) * mm});
            skLineSegment(sketch, "E225.5", {"start": v(13.1, -121.79) * mm, "end": v(18.85, -125.71) * mm});
            skArc(sketch, "E225.6", {"start": v(10.61, -118.09) * mm, "mid": v(11.5, -120.18) * mm, "end": v(13.1, -121.79) * mm});
            skLineSegment(sketch, "E225.7", {"start": v(4.48, -89.5) * mm, "end": v(10.61, -118.09) * mm});
            skLineSegment(sketch, "E225.8", {"start": v(22.23, -126.76) * mm, "end": v(26.18, -126.76) * mm});
            skArc(sketch, "E225.9", {"start": v(26.18, -126.76) * mm, "mid": v(28.53, -126.28) * mm, "end": v(30.5, -124.91) * mm});
            skLineSegment(sketch, "E225.10", {"start": v(30.5, -124.91) * mm, "end": v(32.32, -123.02) * mm});
            skLineSegment(sketch, "E225.11", {"start": v(32.32, -123.02) * mm, "end": v(30.46, -128.38) * mm});
            skArc(sketch, "E225.12", {"start": v(27.85, -130.89) * mm, "mid": v(29.46, -129.94) * mm, "end": v(30.46, -128.38) * mm});
            skLineSegment(sketch, "E225.13", {"start": v(27.85, -130.89) * mm, "end": v(20.54, -133.12) * mm});
            skLineSegment(sketch, "E226.0", {"start": v(-5.97, -99.88) * mm, "end": v(-5.97, -93.24) * mm});
            skLineSegment(sketch, "E226.1", {"start": v(-14.02, -125.61) * mm, "end": v(-5.97, -99.88) * mm});
            skArc(sketch, "E226.2", {"start": v(-14.64, -126.98) * mm, "mid": v(-14.29, -126.32) * mm, "end": v(-14.02, -125.61) * mm});
            skLineSegment(sketch, "E226.3", {"start": v(-30.93, -124.03) * mm, "end": v(-31.55, -126.86) * mm});
            skLineSegment(sketch, "E226.4", {"start": v(-33.09, -126.88) * mm, "end": v(-30.93, -124.03) * mm});
            skArc(sketch, "E226.5", {"start": v(-33.09, -126.88) * mm, "mid": v(-33.69, -128.02) * mm, "end": v(-33.9, -129.3) * mm});
            skLineSegment(sketch, "E226.6", {"start": v(-33.9, -132.95) * mm, "end": v(-33.9, -129.3) * mm});
            skArc(sketch, "E226.7", {"start": v(-31.55, -126.86) * mm, "mid": v(-31.44, -129.87) * mm, "end": v(-29.87, -132.45) * mm});
            skLineSegment(sketch, "E226.8", {"start": v(-29.87, -132.45) * mm, "end": v(-27.93, -134.33) * mm});
            skArc(sketch, "E226.9", {"start": v(-27.93, -134.33) * mm, "mid": v(-26, -135.6) * mm, "end": v(-23.75, -136.03) * mm});
            skLineSegment(sketch, "E226.10", {"start": v(-23.75, -136.03) * mm, "end": v(-23.6, -136.03) * mm});
            skArc(sketch, "E226.11", {"start": v(-23.6, -136.03) * mm, "mid": v(-20.68, -135.28) * mm, "end": v(-18.5, -133.2) * mm});
            skLineSegment(sketch, "E226.12", {"start": v(-18.5, -133.2) * mm, "end": v(-14.64, -126.98) * mm});
            skLineSegment(sketch, "E227.0", {"start": v(-0.92, -110.83) * mm, "end": v(-9.37, -131.37) * mm});
            skArc(sketch, "E227.1", {"start": v(-10.57, -132.97) * mm, "mid": v(-9.87, -132.25) * mm, "end": v(-9.37, -131.37) * mm});
            skLineSegment(sketch, "E227.2", {"start": v(-10.57, -132.97) * mm, "end": v(-18.78, -139.52) * mm});
            skArc(sketch, "E227.3", {"start": v(-21.27, -140.39) * mm, "mid": v(-19.95, -140.17) * mm, "end": v(-18.78, -139.52) * mm});
            skArc(sketch, "E227.4", {"start": v(-33.9, -132.95) * mm, "mid": v(-33.59, -134.5) * mm, "end": v(-32.7, -135.8) * mm});
            skLineSegment(sketch, "E227.5", {"start": v(-29.22, -139.24) * mm, "end": v(-32.7, -135.8) * mm});
            skArc(sketch, "E227.6", {"start": v(-29.22, -139.24) * mm, "mid": v(-27.93, -140.1) * mm, "end": v(-26.4, -140.39) * mm});
            skLineSegment(sketch, "E227.7", {"start": v(-21.27, -140.39) * mm, "end": v(-26.4, -140.39) * mm});
            skLineSegment(sketch, "E228.0", {"start": v(-11.83, -83.18) * mm, "end": v(-7.25, -71.59) * mm});
            skLineSegment(sketch, "E228.1", {"start": v(-16.08, -98.13) * mm, "end": v(-11.83, -83.18) * mm});
            skArc(sketch, "E228.2", {"start": v(-18.01, -101.1) * mm, "mid": v(-16.82, -99.76) * mm, "end": v(-16.08, -98.13) * mm});
            skArc(sketch, "E228.3", {"start": v(-23.3, -109.33) * mm, "mid": v(-22, -109.12) * mm, "end": v(-20.83, -108.49) * mm});
            skLineSegment(sketch, "E228.4", {"start": v(-15.72, -104.5) * mm, "end": v(-20.83, -108.49) * mm});
            skArc(sketch, "E228.5", {"start": v(-15.72, -104.5) * mm, "mid": v(-15.14, -103.95) * mm, "end": v(-14.69, -103.3) * mm});
            skLineSegment(sketch, "E228.6", {"start": v(-8.62, -92.48) * mm, "end": v(-14.69, -103.3) * mm});
            skLineSegment(sketch, "E228.7", {"start": v(-23.3, -109.33) * mm, "end": v(-26.74, -109.33) * mm});
            skArc(sketch, "E228.8", {"start": v(-29.81, -107.9) * mm, "mid": v(-28.44, -108.96) * mm, "end": v(-26.74, -109.33) * mm});
            skLineSegment(sketch, "E228.9", {"start": v(-29.81, -107.9) * mm, "end": v(-32.3, -104.92) * mm});
            skLineSegment(sketch, "E228.10", {"start": v(-32.3, -104.92) * mm, "end": v(-28.15, -106.12) * mm});
            skArc(sketch, "E228.11", {"start": v(-28.15, -106.12) * mm, "mid": v(-25.26, -106.22) * mm, "end": v(-22.65, -104.96) * mm});
            skLineSegment(sketch, "E228.12", {"start": v(-22.65, -104.96) * mm, "end": v(-18.01, -101.1) * mm});
            skLineSegment(sketch, "E229.0", {"start": v(-11.47, -64.27) * mm, "end": v(-11.47, -61.47) * mm});
            skArc(sketch, "E229.1", {"start": v(-13.36, -68.64) * mm, "mid": v(-11.96, -66.65) * mm, "end": v(-11.47, -64.27) * mm});
            skLineSegment(sketch, "E229.2", {"start": v(-16.58, -71.66) * mm, "end": v(-13.36, -68.64) * mm});
            skArc(sketch, "E229.3", {"start": v(-22.8, -72.9) * mm, "mid": v(-19.51, -73.17) * mm, "end": v(-16.58, -71.66) * mm});
            skArc(sketch, "E229.4", {"start": v(-24.4, -75.15) * mm, "mid": v(-23.21, -75.81) * mm, "end": v(-21.87, -76.04) * mm});
            skLineSegment(sketch, "E229.5", {"start": v(-17.18, -76.04) * mm, "end": v(-21.87, -76.04) * mm});
            skArc(sketch, "E229.6", {"start": v(-17.18, -76.04) * mm, "mid": v(-15.86, -75.82) * mm, "end": v(-14.68, -75.16) * mm});
            skLineSegment(sketch, "E229.7", {"start": v(-8.8, -70.44) * mm, "end": v(-14.68, -75.16) * mm});
            skLineSegment(sketch, "E229.8", {"start": v(-24.4, -75.15) * mm, "end": v(-27.57, -72.56) * mm});
            skArc(sketch, "E229.9", {"start": v(-29.05, -69.46) * mm, "mid": v(-28.66, -71.17) * mm, "end": v(-27.57, -72.56) * mm});
            skLineSegment(sketch, "E229.10", {"start": v(-29.05, -69.46) * mm, "end": v(-29.05, -69) * mm});
            skLineSegment(sketch, "E229.11", {"start": v(-29.05, -69) * mm, "end": v(-28.53, -69.7) * mm});
            skArc(sketch, "E229.12", {"start": v(-28.53, -69.7) * mm, "mid": v(-27.32, -70.93) * mm, "end": v(-25.82, -71.76) * mm});
            skLineSegment(sketch, "E229.13", {"start": v(-25.82, -71.76) * mm, "end": v(-22.8, -72.9) * mm});
            skLineSegment(sketch, "E230.0", {"start": v(-16, -61.62) * mm, "end": v(-11.87, -58.57) * mm});
            skArc(sketch, "E230.1", {"start": v(-20.69, -62.69) * mm, "mid": v(-18.23, -62.64) * mm, "end": v(-16, -61.62) * mm});
            skLineSegment(sketch, "E230.2", {"start": v(-20.85, -62.66) * mm, "end": v(-20.69, -62.69) * mm});
            skLineSegment(sketch, "E230.3", {"start": v(-13.11, -60.71) * mm, "end": v(-15.25, -62.53) * mm});
            skArc(sketch, "E230.4", {"start": v(-17.84, -63.48) * mm, "mid": v(-16.46, -63.24) * mm, "end": v(-15.25, -62.53) * mm});
            skLineSegment(sketch, "E230.5", {"start": v(-17.84, -63.48) * mm, "end": v(-18.42, -63.48) * mm});
            skArc(sketch, "E230.6", {"start": v(-20.85, -62.66) * mm, "mid": v(-19.7, -63.27) * mm, "end": v(-18.42, -63.48) * mm});
            skLineSegment(sketch, "E231", {"start": v(-11.87, -58.57) * mm, "end": v(-11.24, -58.19) * mm});
            skLineSegment(sketch, "E232", {"start": v(-13.11, -60.71) * mm, "end": v(-11.47, -59.18) * mm});
            skLineSegment(sketch, "E233", {"start": v(-11.47, -59.18) * mm, "end": v(-11.47, -61.47) * mm});
            skLineSegment(sketch, "E234", {"start": v(-8.8, -70.44) * mm, "end": v(-6.58, -68.9) * mm});
            skLineSegment(sketch, "E235", {"start": v(-6.58, -68.9) * mm, "end": v(-7.25, -71.59) * mm});
            skLineSegment(sketch, "E236", {"start": v(-5.97, -93.24) * mm, "end": v(-5.97, -87.29) * mm});
            skLineSegment(sketch, "E237", {"start": v(-5.97, -87.29) * mm, "end": v(-8.62, -92.48) * mm});
            skLineSegment(sketch, "E238", {"start": v(0.93, -110.85) * mm, "end": v(-0.18, -108) * mm});
            skLineSegment(sketch, "E239", {"start": v(-0.18, -108) * mm, "end": v(-0.92, -110.83) * mm});
            skLineSegment(sketch, "E240", {"start": v(6.04, -88.49) * mm, "end": v(4.03, -87) * mm});
            skLineSegment(sketch, "E241", {"start": v(4.03, -87) * mm, "end": v(4.48, -89.5) * mm});
            skLineSegment(sketch, "E242", {"start": v(10.05, -65.79) * mm, "end": v(7.63, -62.4) * mm});
            skLineSegment(sketch, "E243", {"start": v(7.63, -62.4) * mm, "end": v(7.94, -66.24) * mm});
            skPoint(sketch, "E244.visualSharp", {"position": v(7.98, -66.73) * mm});
            skArc(sketch, "E244.filletArc", {"start": v(7.94, -66.24) * mm, "mid": v(8, -66.73) * mm, "end": v(8.11, -67.2) * mm});
            skLineSegment(sketch, "E245", {"start": v(26.3, -73.04) * mm, "end": v(23.39, -74.18) * mm});
            skPoint(sketch, "E245.endSnap0", {"position": v(23.39, -74.96) * mm});
            skLineSegment(sketch, "E246", {"start": v(23.39, -74.18) * mm, "end": v(20.46, -73.56) * mm});
            skPoint(sketch, "E246.endSnap0", {"position": v(18.3, -73.56) * mm});
            skLineSegment(sketch, "E247", {"start": v(20.46, -73.56) * mm, "end": v(15.15, -70.11) * mm});
            skLineSegment(sketch, "E248", {"start": v(15.15, -70.11) * mm, "end": v(8.7, -59.12) * mm});
            skLineSegment(sketch, "E249", {"start": v(37.33, -94.32) * mm, "end": v(33.32, -97.32) * mm});
            skLineSegment(sketch, "E250", {"start": v(33.32, -97.32) * mm, "end": v(23.52, -98.16) * mm});
            skLineSegment(sketch, "E251", {"start": v(23.52, -98.16) * mm, "end": v(15.62, -92.48) * mm});
            skLineSegment(sketch, "E252", {"start": v(15.62, -92.48) * mm, "end": v(7.85, -84.48) * mm});
            skLineSegment(sketch, "E253", {"start": v(7.85, -84.48) * mm, "end": v(0.6, -60.04) * mm});
            skPoint(sketch, "E253.endSnap0", {"position": v(0.25, -60.04) * mm});
            skLineSegment(sketch, "E254", {"start": v(32.32, -123.02) * mm, "end": v(28.3, -128.38) * mm});
            skLineSegment(sketch, "E255", {"start": v(28.3, -128.38) * mm, "end": v(19.37, -129.95) * mm});
            skLineSegment(sketch, "E256", {"start": v(19.37, -129.95) * mm, "end": v(10.12, -123.3) * mm});
            skLineSegment(sketch, "E257", {"start": v(10.12, -123.3) * mm, "end": v(6.05, -115.7) * mm});
            skLineSegment(sketch, "E258", {"start": v(6.05, -115.7) * mm, "end": v(0.67, -95.52) * mm});
            skLineSegment(sketch, "E259", {"start": v(0.67, -95.52) * mm, "end": v(-2.3, -83.17) * mm});
            skLineSegment(sketch, "E260", {"start": v(-2.3, -83.17) * mm, "end": v(0.25, -60.04) * mm});
            skLineSegment(sketch, "E261", {"start": v(-30.93, -124.03) * mm, "end": v(-32.96, -129.3) * mm});
            skLineSegment(sketch, "E262", {"start": v(-32.96, -129.3) * mm, "end": v(-31.22, -134.27) * mm});
            skLineSegment(sketch, "E263", {"start": v(-31.22, -134.27) * mm, "end": v(-27.08, -137.6) * mm});
            skLineSegment(sketch, "E264", {"start": v(-27.08, -137.6) * mm, "end": v(-21.76, -138.08) * mm});
            skLineSegment(sketch, "E265", {"start": v(-21.76, -138.08) * mm, "end": v(-17.97, -136.16) * mm});
            skLineSegment(sketch, "E266", {"start": v(-17.97, -136.16) * mm, "end": v(-13.15, -129.93) * mm});
            skLineSegment(sketch, "E267", {"start": v(-13.15, -129.93) * mm, "end": v(-6.34, -114.26) * mm});
            skLineSegment(sketch, "E268", {"start": v(-6.34, -114.26) * mm, "end": v(-1.8, -100.24) * mm});
            skLineSegment(sketch, "E269", {"start": v(-1.8, -100.24) * mm, "end": v(-2.3, -83.17) * mm});
            skLineSegment(sketch, "E270", {"start": v(-32.3, -104.92) * mm, "end": v(-26.9, -107.9) * mm});
            skLineSegment(sketch, "E271", {"start": v(-26.9, -107.9) * mm, "end": v(-22.51, -107.34) * mm});
            skLineSegment(sketch, "E272", {"start": v(-22.51, -107.34) * mm, "end": v(-15.96, -102.05) * mm});
            skLineSegment(sketch, "E273", {"start": v(-15.96, -102.05) * mm, "end": v(-13.97, -98.29) * mm});
            skLineSegment(sketch, "E274", {"start": v(-13.97, -98.29) * mm, "end": v(-10.16, -89.46) * mm});
            skLineSegment(sketch, "E275", {"start": v(-10.16, -89.46) * mm, "end": v(-4.08, -73.24) * mm});
            skLineSegment(sketch, "E276", {"start": v(-4.08, -73.24) * mm, "end": v(-1.34, -61.9) * mm});
            skLineSegment(sketch, "E277", {"start": v(-1.34, -61.9) * mm, "end": v(-1.34, -60) * mm});
            skLineSegment(sketch, "E278", {"start": v(-29.05, -69) * mm, "end": v(-28.53, -70.44) * mm});
            skLineSegment(sketch, "E279", {"start": v(-28.53, -70.44) * mm, "end": v(-26.59, -72.34) * mm});
            skLineSegment(sketch, "E280", {"start": v(-26.59, -72.34) * mm, "end": v(-23.08, -74.34) * mm});
            skLineSegment(sketch, "E281", {"start": v(-23.08, -74.34) * mm, "end": v(-19.47, -74.71) * mm});
            skLineSegment(sketch, "E282", {"start": v(-19.47, -74.71) * mm, "end": v(-16.63, -74.18) * mm});
            skLineSegment(sketch, "E283", {"start": v(-16.63, -74.18) * mm, "end": v(-10.85, -69.26) * mm});
            skLineSegment(sketch, "E284", {"start": v(-10.85, -69.26) * mm, "end": v(-6.99, -63.88) * mm});
            skLineSegment(sketch, "E285", {"start": v(-6.99, -63.88) * mm, "end": v(-5.3, -60.2) * mm});
            skLineSegment(sketch, "E286", {"start": v(-5.3, -60.2) * mm, "end": v(-5.3, -59.6) * mm});
            skLineSegment(sketch, "E287", {"start": v(12.08, -58.3) * mm, "end": v(12.03, -58.2) * mm});
            skLineSegment(sketch, "E288", {"start": v(12.03, -58.2) * mm, "end": v(12.03, -58.2) * mm});
            skSolve(sketch);
        }
        {
            var Q0;
            {var subQ8=sQuery(id+"F5.wireOp",EDGE,"E131");Q0=makeQuery(id+"F5.imprint","IMPRINT",FACE,{"disambiguationData":[TD([[makeQuery(id+"F5.imprint","IMPRINT",EDGE,{"derivedFrom":subQ8}),-1.0]])]});}
            extrude(context, id + "F6", {"entities" : qUnion([Q0]), "operationType" : NewBodyOperationType.ADD, "depth" : 3.5 * mm});
        }
        {
            var Q0;
            Q0=makeQuery(id+"F5.imprint","IMPRINT",FACE,{"disambiguationData":[TD([[makeQuery(id+"F5.imprint","IMPRINT",EDGE,{"derivedFrom":sQuery(id+"F5.wireOp",EDGE,"E228.0")}),-1.0]])]});
            var Q1;
            {var subQ8=sQuery(id+"F5.wireOp",EDGE,"E131");Q1=makeQuery(id+"F5.imprint","IMPRINT",FACE,{"disambiguationData":[TD([[makeQuery(id+"F5.imprint","IMPRINT",EDGE,{"derivedFrom":subQ8}),-1.0]])]});}
            var Q2;
            Q2=makeQuery(id+"F5.imprint","IMPRINT",FACE,{"disambiguationData":[TD([[makeQuery(id+"F5.imprint","IMPRINT",EDGE,{"derivedFrom":sQuery(id+"F5.wireOp",EDGE,"E224.0")}),-1.0]])]});
            var Q3;
            Q3=makeQuery(id+"F5.imprint","IMPRINT",FACE,{"disambiguationData":[TD([[makeQuery(id+"F5.imprint","IMPRINT",EDGE,{"derivedFrom":sQuery(id+"F5.wireOp",EDGE,"E223.0")}),-1.0]])]});
            extrude(context, id + "F7", {"entities" : qUnion([Q0, Q1, Q2, Q3]), "depth" : 3 * mm});
        }
        {
            var Q0;
            Q0=makeQuery(id+"F5.imprint","IMPRINT",FACE,{"disambiguationData":[TD([[makeQuery(id+"F5.imprint","IMPRINT",EDGE,{"derivedFrom":sQuery(id+"F5.wireOp",EDGE,"E225.0")}),-1.0]])]});
            var Q1;
            Q1=makeQuery(id+"F5.imprint","IMPRINT",FACE,{"disambiguationData":[TD([[makeQuery(id+"F5.imprint","IMPRINT",EDGE,{"derivedFrom":sQuery(id+"F5.wireOp",EDGE,"E226.0")}),-1.0]])]});
            var Q2;
            Q2=makeQuery(id+"F5.imprint","IMPRINT",FACE,{"disambiguationData":[TD([[makeQuery(id+"F5.imprint","IMPRINT",EDGE,{"derivedFrom":sQuery(id+"F5.wireOp",EDGE,"E223.5")}),-1.0]])]});
            var Q3;
            Q3=makeQuery(id+"F5.imprint","IMPRINT",FACE,{"disambiguationData":[TD([[makeQuery(id+"F5.imprint","IMPRINT",EDGE,{"derivedFrom":sQuery(id+"F5.wireOp",EDGE,"E229.0")}),-1.0]])]});
            extrude(context, id + "F8", {"entities" : qUnion([Q0, Q1, Q2, Q3]), "depth" : 3 * mm});
        }
    });
